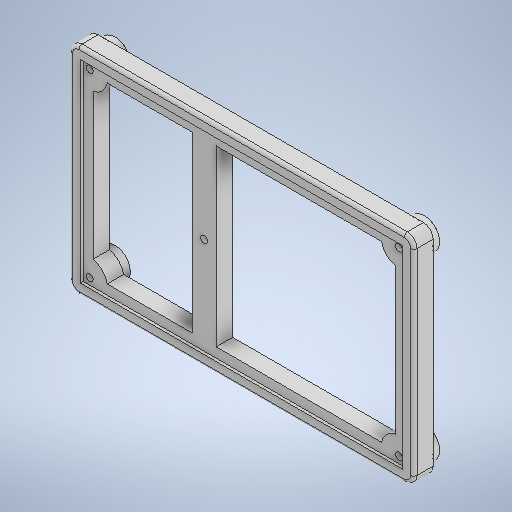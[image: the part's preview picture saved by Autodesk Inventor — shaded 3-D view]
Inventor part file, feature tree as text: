
AUTODESK INVENTOR PART (.ipt)
format: ipt  version: 2025 (Build 290162000, 162)  size: 405,504 bytes
history: native  units: in
note: dims shown in document units (in); Inventor stores cm internally (conversion verified against a paired STEP export)
features: fillet x7, sketch x7, extrude x6, hole x1
ambient origin geometry x8: Origin, YZ Plane, XZ Plane, XY Plane, X Axis, Y Axis, Z Axis, Center Point
bodies: Solid1 (feature_tree)
feature tree (21):
  extrude  "Extrusion1"  Depth=4.9606in
  extrude  "Extrusion2"  Depth=0.3543in
  hole  "Hole1"  [1 undecoded]
  extrude  "Extrusion3"  Depth=7.8819in
  extrude  "Extrusion4"  Depth=0.0709in TaperAngle=0.0deg
  fillet  "Fillet1"  Radius=3.7795in
  fillet  "Fillet2"  Radius=2.2047in
  fillet  "Fillet3"  Radius=3.7795in
  extrude  "Extrusion7"  Depth=3.7795in
  extrude  "Extrusion8"  Depth=0.0276in
  fillet  "Fillet4"  Radius=2.2047in
  fillet  "Fillet5"  Radius=0.9843in
  fillet  "Fillet6"  [1 undecoded]
  fillet  "Fillet7"  Radius=0.1575in
  sketch  "Sketch1"  dims[d0=8.1102in d1=4.9606in]
  sketch  "Sketch2"  dims[d2=0.3543in d3=0.3543in]
  sketch  "Sketch3"  dims[d4=0.5906in d5=0.689in]
  sketch  "Sketch4"  dims[d6=0.4724in d7=0.0in d8=7.8819in]
  sketch  "Sketch5"  dims[d9=4.7323in d10=0.0709in d11=0.0in d12=3.7795in d13=2.2047in d14=3.7795in]
  sketch  "Sketch9"  dims[d15=2.2047in d16=3.7795in]
  sketch  "Sketch10"  dims[d17=2.2047in d18=3.7795in d19=2.2047in d20=0.1701in d21=0.2362in d22=0.1732in d23=0.0787in d24=90.0deg d25=0.315in d26=0.8108in d27=0.9843in d28=0.0in d29=0.1575in d30=0.1575in d31=0.3937in d32=0.0in d33=0.3937in d34=0.0in d47=0.2362in d48=0.2362in d49=0.0787in d51=0.2362in d52=-0.1031in d53=0.6575in d54=0.6575in d55=0.6575in d56=0.6575in d57=0.0591in d58=0.0in d59=0.0276in d60=0.0276in d61=0.0276in d62=0.0276in]
note: 2 required parameter values undecoded (feature->parameter linkage not recoverable at this tier; creation-order binding heuristic only, values carry confidence <= 0.55)
